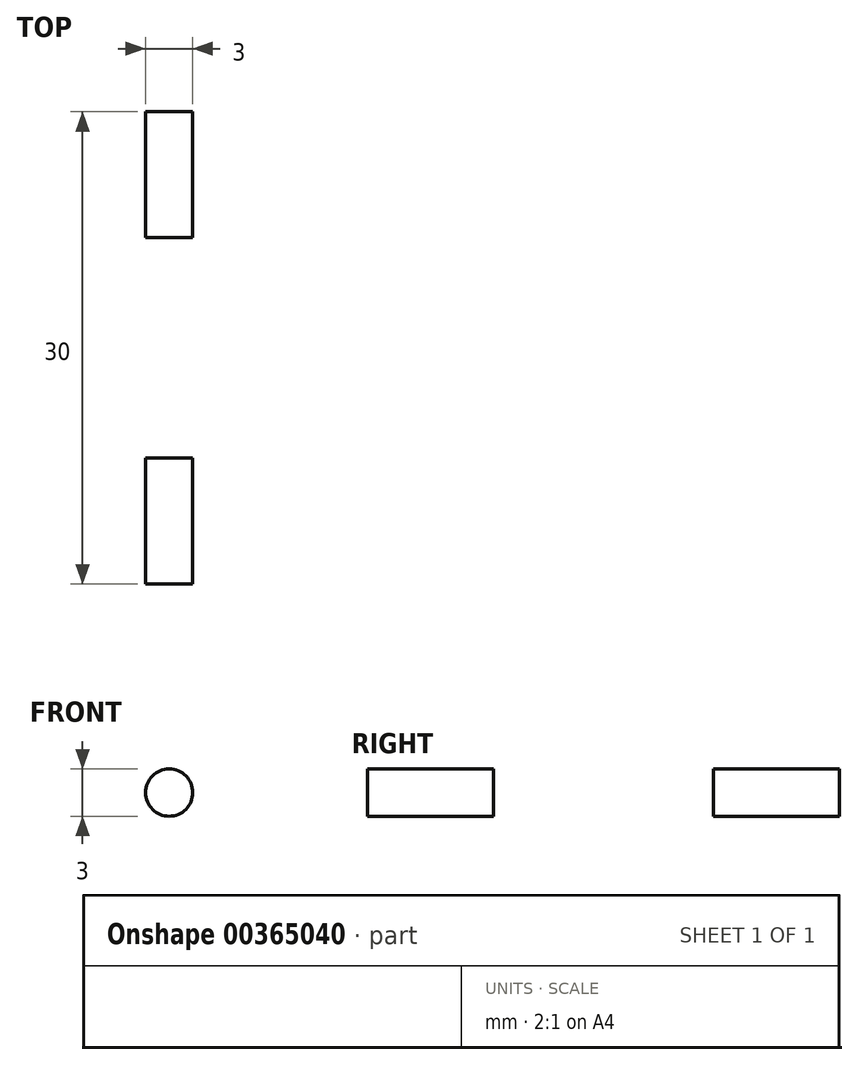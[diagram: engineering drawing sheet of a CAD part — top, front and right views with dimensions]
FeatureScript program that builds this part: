
annotation { "Feature Type Name" : "Feature", "Feature Type Description" : "" }
export const myFeature = defineFeature(function(context is Context, id is Id, definition is map)
    precondition{}
    {
        {
            var Q0;
            Q0=qCreatedBy(makeId("Top.planeOp"),FACE);
            var sketch = newSketch(context, id + "F0", { "sketchPlane" : qUnion([Q0])});
            skLineSegment(sketch, "E0.bottom", {"start": v(123.95, -15) * mm, "end": v(-123.95, -15) * mm});
            skLineSegment(sketch, "E0.left", {"start": v(123.95, -15) * mm, "end": v(123.95, -7) * mm});
            skPoint(sketch, "E0.middle", {"position": v(0, 0) * mm});
            skLineSegment(sketch, "E1.bottom", {"start": v(84.02, -4) * mm, "end": v(-36.05, -4) * mm});
            skLineSegment(sketch, "E1.top", {"start": v(123.95, -7) * mm, "end": v(-36.05, -7) * mm});
            skLineSegment(sketch, "E1.right", {"start": v(-36.05, -4) * mm, "end": v(-36.05, -7) * mm});
            skLineSegment(sketch, "E2", {"start": v(83.96, 4) * mm, "end": v(83.95, 4) * mm});
            skLineSegment(sketch, "E3.right", {"start": v(84.02, 4) * mm, "end": v(84.02, -4) * mm});
            skLineSegment(sketch, "E4", {"start": v(-123.95, 15) * mm, "end": v(-123.95, -15) * mm});
            skLineSegment(sketch, "E5", {"start": v(-123.95, 15) * mm, "end": v(123.95, 15) * mm});
            skLineSegment(sketch, "E6", {"start": v(123.95, 15) * mm, "end": v(123.95, 7) * mm});
            skLineSegment(sketch, "E7", {"start": v(-36.05, 7) * mm, "end": v(123.95, 7) * mm});
            skLineSegment(sketch, "E8", {"start": v(-36.05, 7) * mm, "end": v(-36.05, 4) * mm});
            skLineSegment(sketch, "E9", {"start": v(-36.05, 4) * mm, "end": v(84.02, 4) * mm});
            skSolve(sketch);
        }
        {
            var Q0;
            Q0=makeQuery(id+"F0.imprint","IMPRINT",FACE,{"disambiguationData":[TD([[makeQuery(id+"F0.imprint","IMPRINT",EDGE,{"derivedFrom":sQuery(id+"F0.wireOp",EDGE,"E0.bottom")}),-1.0]])]});
            extrude(context, id + "F1", {"entities" : qUnion([Q0]), "depth" : 4 * mm});
        }
        {
            var Q0;
            Q0=makeQuery(id+"F1.opExtrude","CAP_FACE",FACE,{"disambiguationData":[OSD([sQuery(id+"F0.wireOp",EDGE,"E0.bottom"),sQuery(id+"F0.wireOp",EDGE,"E0.left"),sQuery(id+"F0.wireOp",EDGE,"E1.bottom"),sQuery(id+"F0.wireOp",EDGE,"E1.top"),sQuery(id+"F0.wireOp",EDGE,"E1.right"),sQuery(id+"F0.wireOp",EDGE,"E3.right"),sQuery(id+"F0.wireOp",EDGE,"E4"),sQuery(id+"F0.wireOp",EDGE,"E5"),sQuery(id+"F0.wireOp",EDGE,"E6"),sQuery(id+"F0.wireOp",EDGE,"E7"),sQuery(id+"F0.wireOp",EDGE,"E8"),sQuery(id+"F0.wireOp",EDGE,"E9")])],"isStart":false});
            var sketch = newSketch(context, id + "F2", { "sketchPlane" : qUnion([Q0])});
            skLineSegment(sketch, "E10.bottom", {"start": v(123.95, 15) * mm, "end": v(83.96, 15) * mm});
            skLineSegment(sketch, "E10.top", {"start": v(123.95, 7) * mm, "end": v(83.96, 7) * mm});
            skLineSegment(sketch, "E10.left", {"start": v(123.95, 15) * mm, "end": v(123.95, 7) * mm});
            skLineSegment(sketch, "E10.right", {"start": v(83.96, 15) * mm, "end": v(83.96, 7) * mm});
            skLineSegment(sketch, "E11.bottom", {"start": v(123.95, -7) * mm, "end": v(83.8, -7) * mm});
            skLineSegment(sketch, "E11.top", {"start": v(123.95, -15) * mm, "end": v(83.8, -15) * mm});
            skLineSegment(sketch, "E11.left", {"start": v(123.95, -7) * mm, "end": v(123.95, -15) * mm});
            skLineSegment(sketch, "E11.right", {"start": v(83.8, -7) * mm, "end": v(83.8, -15) * mm});
            skSolve(sketch);
        }
        {
            var Q0;
            Q0 = qSketchRegion(id + "F2", true);
            extrude(context, id + "F3", {"entities" : qUnion([Q0]), "operationType" : NewBodyOperationType.ADD, "depth" : 4 * mm});
        }
        {
            var Q0;
            Q0 = qSketchRegion(id + "F2", true);
            extrude(context, id + "F4", {"entities" : qUnion([Q0]), "operationType" : NewBodyOperationType.ADD, "depth" : 4 * mm});
        }
        {
            var Q0;
            Q0=makeQuery(id+"F3.boolean.opBoolean","MERGE",FACE,{"derivedFrom":[makeQuery(id+"F1.opExtrude","SWEPT_FACE",FACE,{"disambiguationData":[OSD([sQuery(id+"F0.wireOp",EDGE,"E0.bottom")])]}),makeQuery(id+"F3.opExtrude","SWEPT_FACE",FACE,{"disambiguationData":[OSD([sQuery(id+"F2.wireOp",EDGE,"E11.top")])]})]});
            var sketch = newSketch(context, id + "F5", { "sketchPlane" : qUnion([Q0])});
            skLineSegment(sketch, "E12.bottom", {"start": v(123.95, 8) * mm, "end": v(108.95, 8) * mm});
            skLineSegment(sketch, "E12.top", {"start": v(123.95, 0) * mm, "end": v(108.95, 0) * mm});
            skLineSegment(sketch, "E12.left", {"start": v(123.95, 8) * mm, "end": v(123.95, 0) * mm});
            skLineSegment(sketch, "E12.right", {"start": v(108.95, 8) * mm, "end": v(108.95, 0) * mm});
            skCircle(sketch, "E13", {"center": v(108.95, 4) * mm, "radius": 1.5 * mm});
            skSolve(sketch);
        }
        {
            var Q0;
            {var subQ0=sQuery(id+"F5.wireOp",EDGE,"E13");var subQ1=sQuery(id+"F5.wireOp",EDGE,"E12.right");var subQ2=makeQuery(id+"F5.imprint","INTERSECT",VERTEX,{"disambiguationData":[OD(0.0)],"derivedFrom":[subQ1,subQ0]});Q0=makeQuery(id+"F5.imprint","IMPRINT",FACE,{"disambiguationData":[TD([[makeQuery(id+"F5.imprint","IMPRINT",EDGE,{"disambiguationData":[TD([[subQ2,-1.0]])],"derivedFrom":subQ1}),1.0]])]});}
            var Q1;
            {var subQ0=sQuery(id+"F5.wireOp",EDGE,"E13");var subQ1=sQuery(id+"F5.wireOp",EDGE,"E12.right");var subQ2=makeQuery(id+"F5.imprint","INTERSECT",VERTEX,{"disambiguationData":[OD(0.0)],"derivedFrom":[subQ1,subQ0]});Q1=makeQuery(id+"F5.imprint","IMPRINT",FACE,{"disambiguationData":[TD([[makeQuery(id+"F5.imprint","IMPRINT",EDGE,{"disambiguationData":[TD([[subQ2,-1.0]])],"derivedFrom":subQ1}),-1.0]])]});}
            var Q2;
            Q2=sQuery(id+"F5.wireOp",EDGE,"E13");
            extrude(context, id + "F6", {"entities" : qUnion([Q0, Q1]), "operationType" : NewBodyOperationType.REMOVE, "surfaceEntities" : qUnion([Q2]), "oppositeDirection" : true, "depth" : 101 * mm});
        }
    });
